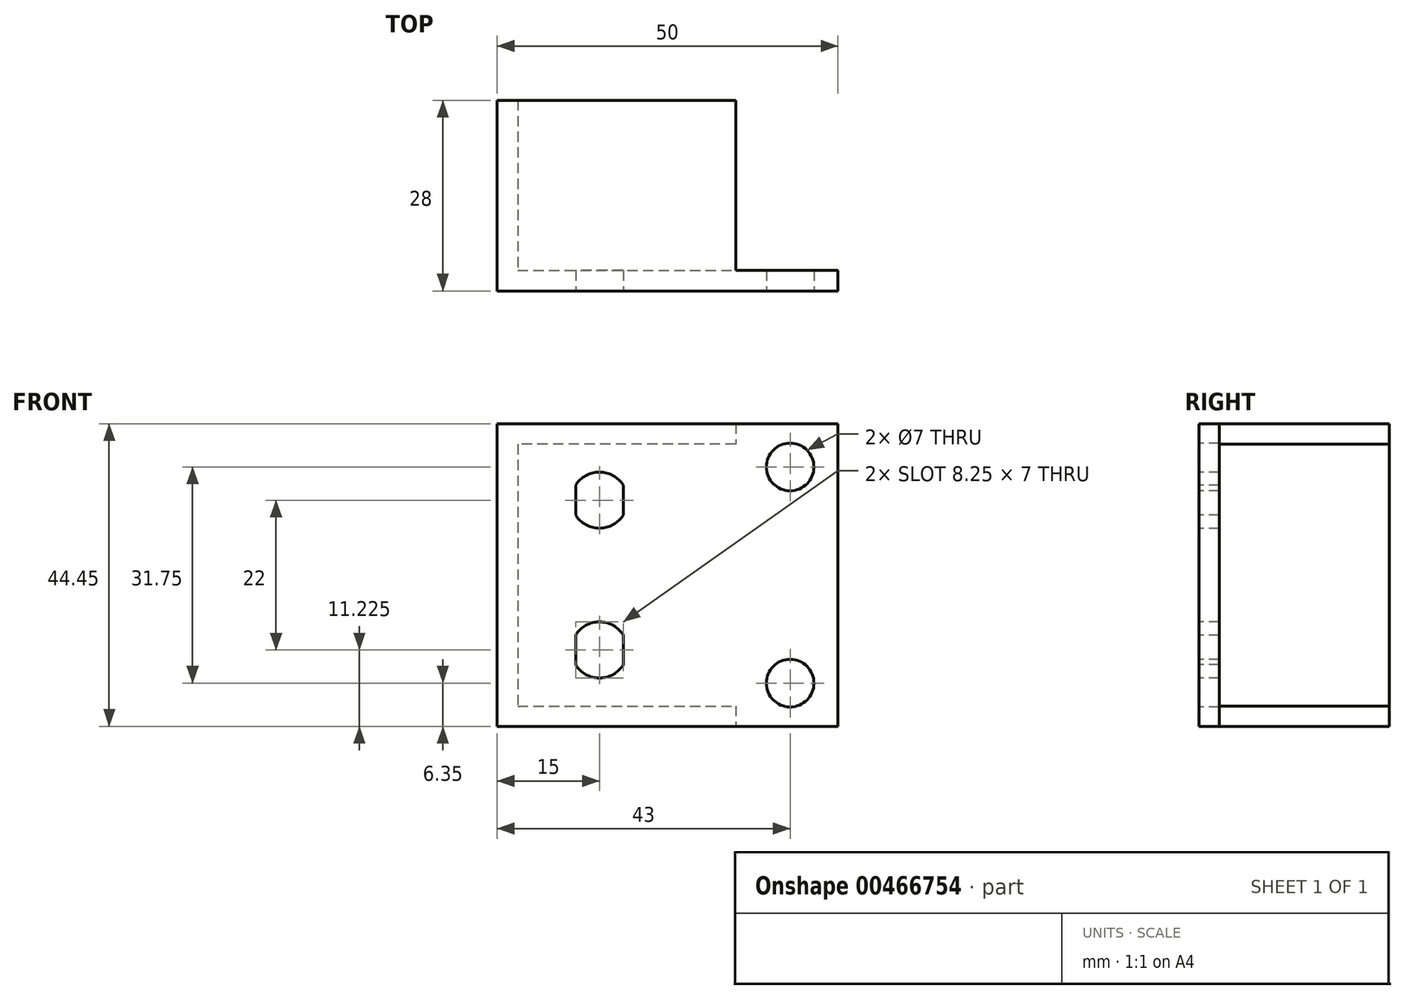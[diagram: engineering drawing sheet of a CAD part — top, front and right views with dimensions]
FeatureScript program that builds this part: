
annotation { "Feature Type Name" : "Feature", "Feature Type Description" : "" }
export const myFeature = defineFeature(function(context is Context, id is Id, definition is map)
    precondition{}
    {
        {
            var Q0;
            Q0=qCreatedBy(makeId("Front.planeOp"),FACE);
            var sketch = newSketch(context, id + "F0", { "sketchPlane" : qUnion([Q0])});
            skLineSegment(sketch, "E0.bottom", {"start": v(0, 0) * mm, "end": v(-50, 0) * mm});
            skLineSegment(sketch, "E0.top", {"start": v(0, 44.45) * mm, "end": v(-50, 44.45) * mm});
            skLineSegment(sketch, "E0.left", {"start": v(0, 0) * mm, "end": v(0, 44.45) * mm});
            skLineSegment(sketch, "E0.right", {"start": v(-50, 0) * mm, "end": v(-50, 44.45) * mm});
            skCircle(sketch, "E1", {"center": v(-7, 38.1) * mm, "radius": 3.5 * mm});
            skCircle(sketch, "E2", {"center": v(-7, 6.35) * mm, "radius": 3.5 * mm});
            skPoint(sketch, "E3", {"position": v(-35, 33.22) * mm});
            skArc(sketch, "E4", {"start": v(-31.5, 35.4) * mm, "mid": v(-35, 37.35) * mm, "end": v(-38.5, 35.4) * mm});
            skLineSegment(sketch, "E5", {"start": v(-50, 22.22) * mm, "end": v(0, 22.23) * mm, "construction": true});
            skLineSegment(sketch, "E6", {"start": v(-38.5, 35.4) * mm, "end": v(-38.5, 31.04) * mm});
            skLineSegment(sketch, "E7", {"start": v(-35, 33.22) * mm, "end": v(-35, 22.22) * mm, "construction": true});
            skLineSegment(sketch, "E8.MirrorCS", {"start": v(-31.5, 35.4) * mm, "end": v(-31.5, 31.04) * mm});
            skArc(sketch, "E9.trimOffspring", {"start": v(-38.5, 31.04) * mm, "mid": v(-35, 29.1) * mm, "end": v(-31.5, 31.04) * mm});
            skArc(sketch, "E10.MirrorCS", {"start": v(-38.5, 13.4) * mm, "mid": v(-35, 15.35) * mm, "end": v(-31.5, 13.4) * mm});
            skLineSegment(sketch, "E11.MirrorCS", {"start": v(-31.5, 9.04) * mm, "end": v(-31.5, 13.4) * mm});
            skArc(sketch, "E12.MirrorCS", {"start": v(-31.5, 9.04) * mm, "mid": v(-35, 7.1) * mm, "end": v(-38.5, 9.04) * mm});
            skLineSegment(sketch, "E13.MirrorCS", {"start": v(-38.5, 9.04) * mm, "end": v(-38.5, 13.4) * mm});
            skSolve(sketch);
        }
        {
            var Q0;
            Q0=makeQuery(id+"F0.imprint","IMPRINT",FACE,{"disambiguationData":[TD([[makeQuery(id+"F0.imprint","IMPRINT",EDGE,{"derivedFrom":sQuery(id+"F0.wireOp",EDGE,"E0.bottom")}),-1.0]])]});
            extrude(context, id + "F1", {"entities" : qUnion([Q0]), "oppositeDirection" : true, "depth" : 3 * mm});
        }
        {
            var Q0;
            Q0=makeQuery(id+"F1.opExtrude","CAP_FACE",FACE,{"disambiguationData":[OSD([sQuery(id+"F0.wireOp",EDGE,"E0.bottom"),sQuery(id+"F0.wireOp",EDGE,"E0.top"),sQuery(id+"F0.wireOp",EDGE,"E0.left"),sQuery(id+"F0.wireOp",EDGE,"E0.right")])],"isStart":false});
            var sketch = newSketch(context, id + "F2", { "sketchPlane" : qUnion([Q0])});
            skLineSegment(sketch, "E14", {"start": v(15, 44.45) * mm, "end": v(15, 41.45) * mm});
            skLineSegment(sketch, "E15", {"start": v(15, 41.45) * mm, "end": v(47, 41.45) * mm});
            skLineSegment(sketch, "E16", {"start": v(47, 41.45) * mm, "end": v(47, 3) * mm});
            skLineSegment(sketch, "E17", {"start": v(47, 3) * mm, "end": v(15, 3) * mm});
            skLineSegment(sketch, "E18", {"start": v(15, 3) * mm, "end": v(15, 0) * mm});
            skSolve(sketch);
        }
        {
            var Q0;
            {var subQ0=sQuery(id+"F2.wireOp",EDGE,"E14");Q0=makeQuery(id+"F2.imprint","IMPRINT",FACE,{"disambiguationData":[TD([[makeQuery(id+"F2.imprint","IMPRINT",EDGE,{"derivedFrom":subQ0}),1.0]])]});}
            extrude(context, id + "F3", {"entities" : qUnion([Q0]), "operationType" : NewBodyOperationType.ADD, "depth" : 25 * mm});
        }
    });
